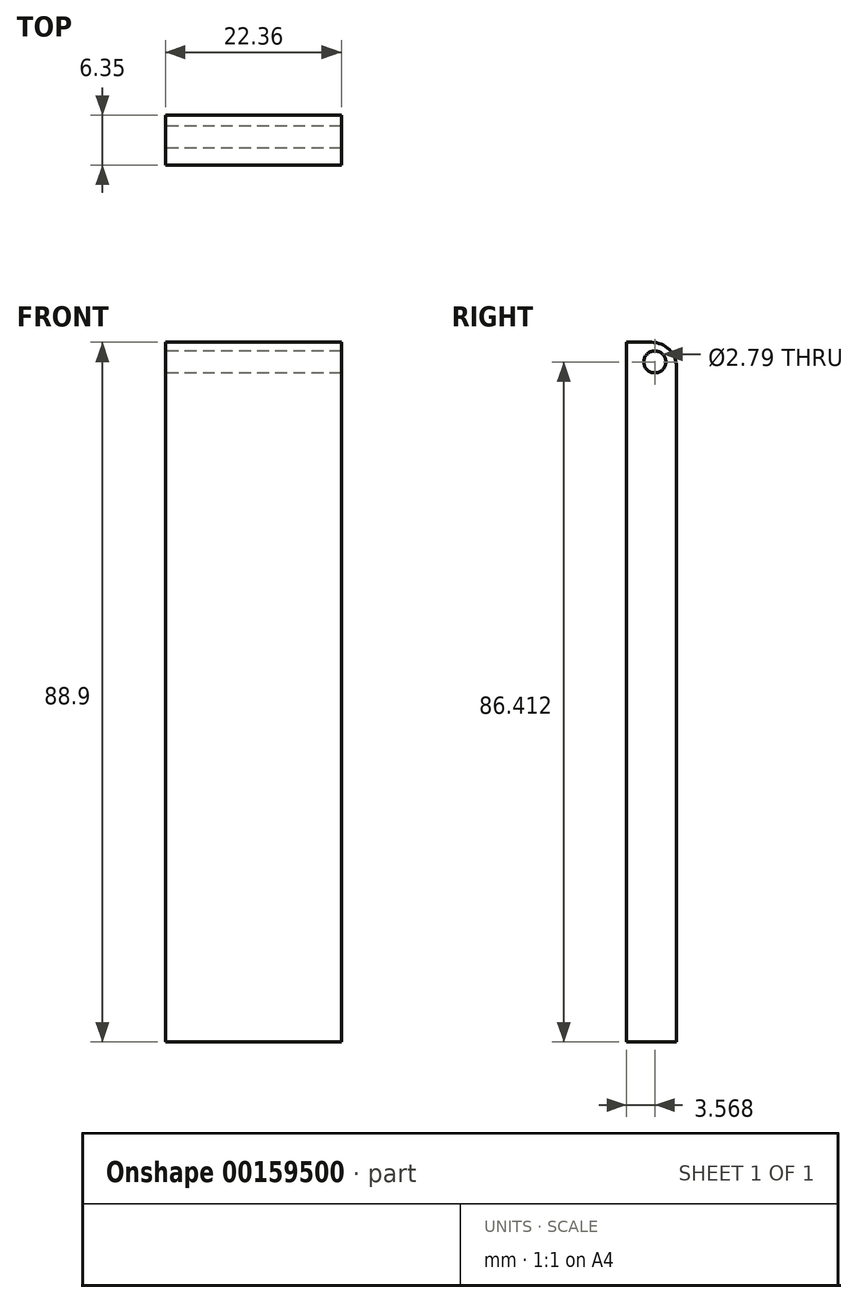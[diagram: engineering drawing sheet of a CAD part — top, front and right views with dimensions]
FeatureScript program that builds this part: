
annotation { "Feature Type Name" : "Feature", "Feature Type Description" : "" }
export const myFeature = defineFeature(function(context is Context, id is Id, definition is map)
    precondition{}
    {
        {
            var Q0;
            Q0=qCreatedBy(makeId("Front.planeOp"),FACE);
            var sketch = newSketch(context, id + "F0", { "sketchPlane" : qUnion([Q0])});
            skLineSegment(sketch, "E0.bottom", {"start": v(11.18, -44.45) * mm, "end": v(-11.18, -44.45) * mm});
            skLineSegment(sketch, "E0.top", {"start": v(11.18, 44.45) * mm, "end": v(-11.18, 44.45) * mm});
            skLineSegment(sketch, "E0.left", {"start": v(11.18, -44.45) * mm, "end": v(11.18, 44.45) * mm});
            skLineSegment(sketch, "E0.right", {"start": v(-11.18, -44.45) * mm, "end": v(-11.18, 44.45) * mm});
            skPoint(sketch, "E0.middle", {"position": v(0, 0) * mm});
            skSolve(sketch);
        }
        {
            var Q0;
            Q0 = qSketchRegion(id + "F0", true);
            extrude(context, id + "F1", {"entities" : qUnion([Q0]), "depth" : 6.35 * mm});
        }
        {
            var Q0;
            Q0=qCreatedBy(makeId("Right.planeOp"),FACE);
            var sketch = newSketch(context, id + "F2", { "sketchPlane" : qUnion([Q0])});
            skCircle(sketch, "E1", {"center": v(-2.78, 41.96) * mm, "radius": 1.4 * mm});
            skSolve(sketch);
        }
        {
            var Q0;
            Q0 = qSketchRegion(id + "F2", true);
            extrude(context, id + "F3", {"entities" : qUnion([Q0]), "operationType" : NewBodyOperationType.REMOVE, "depth" : 15.24 * mm, "hasSecondDirection" : true, "secondDirectionOppositeDirection" : true, "secondDirectionDepth" : 15.24 * mm});
        }
        {
            var Q0;
            Q0=makeQuery(id+"F1.opExtrude","CAP_EDGE",EDGE,{"disambiguationData":[OSD([sQuery(id+"F0.wireOp",EDGE,"E0.top")])],"isStart":true});
            fillet(context, id + "F4", {"entities" : qUnion([Q0]), "radius" : 3.19 * mm, "tangentPropagation" : true, "allowEdgeOverflow" : false});
        }
    });
